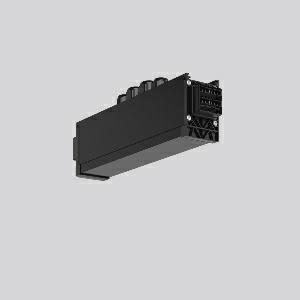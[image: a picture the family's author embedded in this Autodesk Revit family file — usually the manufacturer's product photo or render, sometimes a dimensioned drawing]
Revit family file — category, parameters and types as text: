
# Revit family: linedo_mitteleinspeisung_14pol_s_s_982698_013_2_d857
name_source: partatom
category: Lighting Fixtures
units: mm (PartAtom-declared; Revit-internal decimal feet)

## family parameters
Cut with Voids When Loaded = No
Host = Face
Light Source = No
Part Type = Normal
Room Calculation Point = No
Round Connector Dimension = Use Diameter
Shared = No

## types (1)
- LINEDO_Mitteleinspeisung_14pol_S_S
    Apparent Load = 0 VA
    Default Elevation = 1800 mm
    Description = Series: LINEDO
Middle power feed, 14-pole, connection plug / plug. Housing: extruded aluminium profile, powder-coated. Cover made of plastic, surface like housing. LINEDO plug system, plastic, black. 4 cable glands (2 x M20 and 2 x M25). Cable glands on top. Easy connection for rigid or flexible wires. Especially for use with continuous line modules with high opal diffuser.
Colour: black
Length: 349 mm
Width: 58 mm
Height: 91 mm
Weight: 900 g
    Height = 91 mm
    Lamp = 0 x
    Length = 349 mm
    Luminous efficacy = 0 lm/W
    Manufacturer = RZB
    ModVariant = No
    Model = 982698.013.2
    Mounting Place = Ceiling
    Mounting Type = Surface mounted
    Number of Poles = 1
    OnlyDefault = Yes
    Power Factor = 1
    Product Name = LINEDO_Mitteleinspeisung_14pol_S_S
    Product group = Continuous line luminaire system Linedo IP 54
    ProductGroupID = 314
    Protection Class = Protection class I
    Protection Degree = Degree of protection
    RLX_Detail_Level = 1
    RLX_Emergency_Light_Flux = 0 lm
    RLX_Emergency_Type = 0
    RLX_Emergency_Type_DB = No
    RlxData = <blob elided: 24589 chars, md5=72801e90>
    Standby Power = 0 W
    System Light Flux = 0 lm
    System Power = 0 W
    Type Comments = Product without accessories
    Type Image = 982698.013.2.jpg
    URL = http://relux.com
    VarID = ---
    Voltage = 0 V
    Weight = 0.00 kg
    Width = 58 mm

## geometry (parser evidence)
native form markers: Blend x4, Sweep x11
no freeform markers — native parametric forms only
